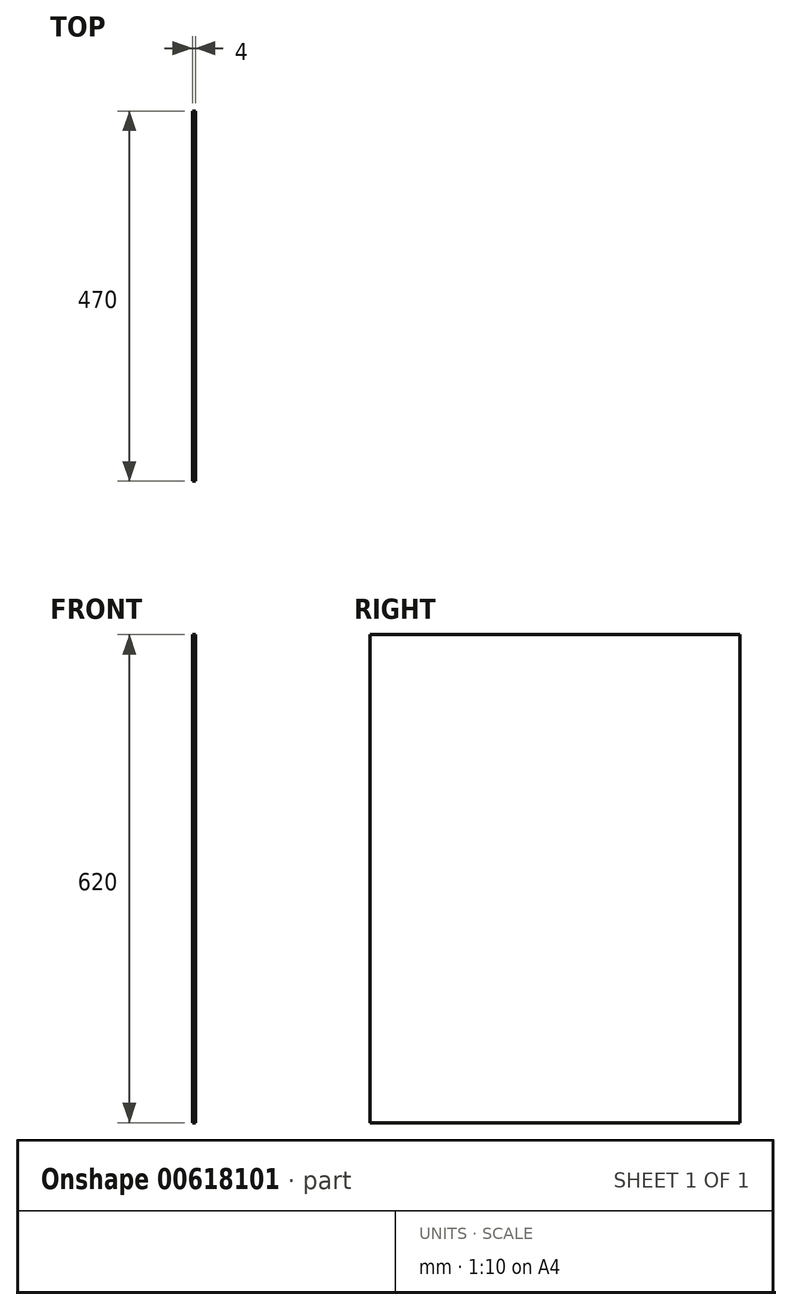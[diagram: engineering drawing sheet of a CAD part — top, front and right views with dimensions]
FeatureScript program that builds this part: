
annotation { "Feature Type Name" : "Feature", "Feature Type Description" : "" }
export const myFeature = defineFeature(function(context is Context, id is Id, definition is map)
    precondition{}
    {
        {
            var Q0;
            Q0=qCreatedBy(makeId("Right.planeOp"),FACE);
            var sketch = newSketch(context, id + "F0", { "sketchPlane" : qUnion([Q0])});
            skLineSegment(sketch, "E0.bottom", {"start": v(-8.8, 560.05) * mm, "end": v(461.2, 560.05) * mm});
            skLineSegment(sketch, "E0.top", {"start": v(-8.8, -59.95) * mm, "end": v(461.2, -59.95) * mm});
            skLineSegment(sketch, "E0.left", {"start": v(-8.8, 560.05) * mm, "end": v(-8.8, -59.95) * mm});
            skLineSegment(sketch, "E0.right", {"start": v(461.2, 560.05) * mm, "end": v(461.2, -59.95) * mm});
            skSolve(sketch);
        }
        {
            var Q0;
            Q0=makeQuery(id+"F0.imprint","IMPRINT",FACE,{"disambiguationData":[TD([[makeQuery(id+"F0.imprint","IMPRINT",EDGE,{"derivedFrom":sQuery(id+"F0.wireOp",EDGE,"E0.bottom")}),-1.0]])]});
            extrude(context, id + "F1", {"entities" : qUnion([Q0]), "depth" : 4 * mm, "offsetDistance" : 25 * mm});
        }
    });
